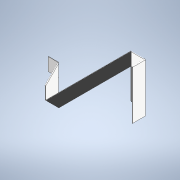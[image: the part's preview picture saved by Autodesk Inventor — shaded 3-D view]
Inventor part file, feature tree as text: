
AUTODESK INVENTOR PART (.ipt)
format: ipt  version: 2021 (Build 250183000, 183)  size: 223,744 bytes
history: native  units: mm
features: sketch x7, other x6, projected_geometry x2, extrude x1
ambient origin geometry x8: Origin, YZ Plane, XZ Plane, XY Plane, X Axis, Y Axis, Z Axis, Center Point
bodies: Solid1 (feature_tree)
feature tree (16):
  extrude  "Extrusion1"  Depth=16.0mm
  other  "Bend Part1"
  other  "Bend Part2"
  other  "Bend Part3"
  other  "Bend Part4"
  other  "Bend Part5"
  other  "Bend Part6"
  sketch  "Sketch1"  dims[d0=300.0mm d1=16.0mm]
  sketch  "Sketch2"  dims[d2=0.5mm d3=0.0mm]
  sketch  "Sketch3"  dims[d4=12.5mm]
  sketch  "Sketch4"  dims[d5=0.1mm d6=90.0deg]
  sketch  "Sketch5"  dims[d7=1.0mm]
  sketch  "Sketch6"  dims[d8=45.0deg]
  projected_geometry  "Projected Loop1"
  sketch  "Sketch7"  dims[d9=0.1mm d10=180.0deg d11=45.0deg d12=15.0mm d13=0.1mm d14=180.0deg d17=88.5mm d18=45.0deg d19=0.1mm d20=180.0deg d21=37.0mm d22=0.1mm d23=180.0deg d24=0.0mm d25=0.1mm d26=180.0deg]
  projected_geometry  "Projected Loop2"
